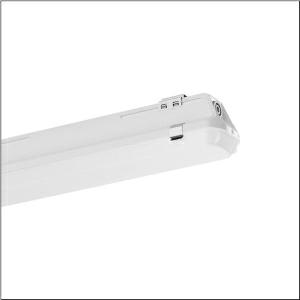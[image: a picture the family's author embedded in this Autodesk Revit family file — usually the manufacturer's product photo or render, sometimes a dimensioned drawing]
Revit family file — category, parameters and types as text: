
# Revit family: monsun_r__21_51fb20dp460b_2c2a
name_source: partatom
category: Lighting Fixtures
units: mm (PartAtom-declared; Revit-internal decimal feet)

## family parameters
Cut with Voids When Loaded = No
Host = Face
Light Source = No
Part Type = Normal
Room Calculation Point = No
Round Connector Dimension = Use Diameter
Shared = No

## types (1)
- --- (1 x LED, 5460 lm, 39.4 W, 4000K)
    Apparent Load = 39 VA
    CIE Flux Codes = 45 75 93 94 100
    Color Rendering = 80
    Color Temperature = 4000K
    Default Elevation = 1800 mm
    Description = Monsun® 21, damp-proof luminaire, chain hanger, primary optical cover: enclosure, of PC, light emission: direct distribution, primary light characteristic: symmetric, installation type: suspended mounting, surface-mounted, horizontal mounting, vertical mounting, LED, rated luminous flux: 5.460lm, luminous efficacy: 139lm/W, light colour: 840, colour temperature: 4000K, control gear: ECG DALI, with terminal, 5-pole, max. 2.5mm², mains connection: 220..240V, AC, 50/60Hz, rated input power: 39W, housing, of glass-fibre reinforced polyester, uncoated, bright grey, incl. chain hanger, length: 1.590mm, width: 90mm, height: 88mm, clip for enclosure, of stainless steel (V2A), ceiling mounting element, of stainless steel (V2A), chain hanger, of stainless steel (V2A), protection rating (complete): IP66, insulation class (complete): insulation class I (protective earthing), certification: CE, ENEC, VDE, UKCA, protection symbol: D, impact resistance: IK08, permissible operating ambient temperature: -25..+35°C, standard: EN 50419, EN 60598-2-1, corresponds to IFS (International Featured Standards) requirements for safety and quality in the food industry, for indoor or canopied outdoor use, no direct snow, no direct sun, no direct rain, contact your sales advisor before using the luminaires in applications with unclear chemical exposure, large temperature fluctuations or condensation-forming humidity, LABS conformity tested according to VDMA 24364:2018-05, packaging unit: 1 piece
    Height = 89 mm
    Lamp = 1 x LED
    Lamp Light Flux = 5460 lm
    Lamp Power = 39.4 W
    Lamp count = 1
    Length = 1590 mm
    Luminous efficacy = 139 lm/W
    Manufacturer = Siteco
    ModVariant = No
    Model = 51FB20DP460B
    Mounting Place = Ceiling
    Mounting Type = Surface mounted
    Number of Poles = 1
    OnlyDefault = Yes
    Power Factor = 1
    Product Name = Monsun® 21
    Product group = damp-proof luminaire
    ProductGroupID = 300
    Protection Class = Protection class I
    Protection Degree = IP 66
    RLX_Detail_Level = 1
    RLX_Emergency_Light_Flux = 0 lm
    RLX_Emergency_Type = 0
    RLX_Emergency_Type_DB = No
    RlxData = <blob elided: 92249 chars, md5=7d65eec4>
    Socket = socket
    Standby Power = 0 W
    System Light Flux = 5460 lm
    System Power = 39 W
    Type Comments = factory setting: luminous flux: 100 % | dim-lin: 254 | 261 mA
    Type Image = l_1006717.jpg
    URL = http://relux.com
    VarID = @adj_134279
    Voltage = 0 V
    Weight = 0.00 kg
    Width = 90 mm

## geometry (parser evidence)
native form markers: Blend x4, Sweep x15
no freeform markers — native parametric forms only
